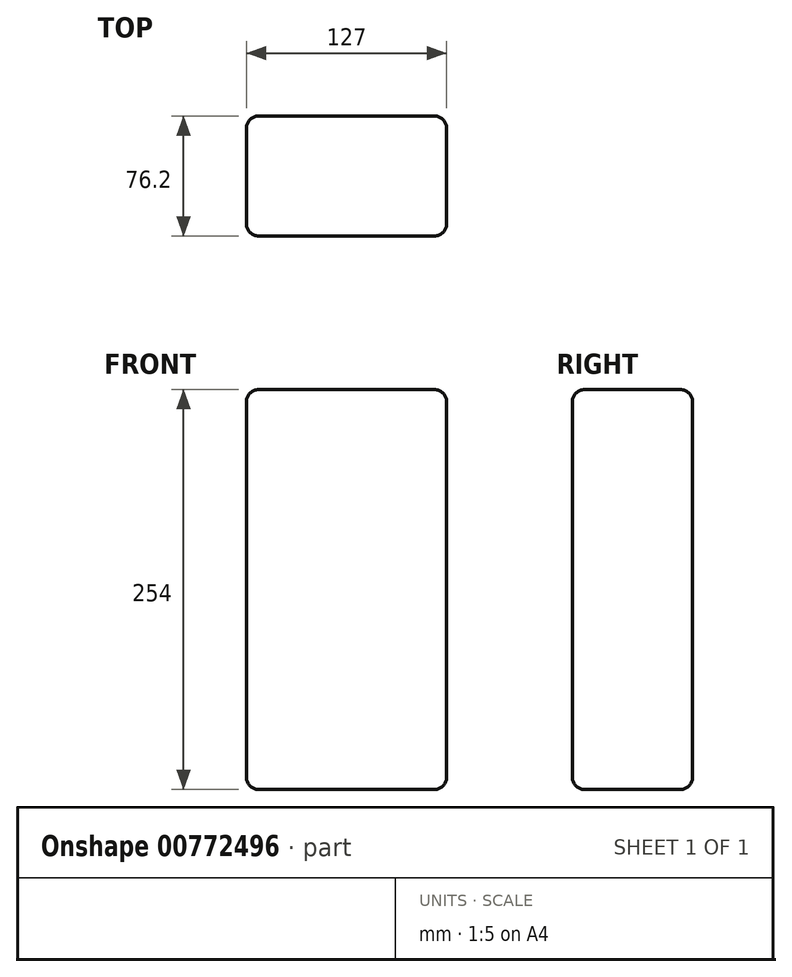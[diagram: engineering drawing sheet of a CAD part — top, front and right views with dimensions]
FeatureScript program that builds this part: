
annotation { "Feature Type Name" : "Feature", "Feature Type Description" : "" }
export const myFeature = defineFeature(function(context is Context, id is Id, definition is map)
    precondition{}
    {
        {
            var Q0;
            Q0=qCreatedBy(makeId("Front.planeOp"),FACE);
            var sketch = newSketch(context, id + "F0", { "sketchPlane" : qUnion([Q0])});
            skLineSegment(sketch, "E0.bottom", {"start": v(63.5, 127) * mm, "end": v(-63.5, 127) * mm});
            skLineSegment(sketch, "E0.top", {"start": v(63.5, -127) * mm, "end": v(-63.5, -127) * mm});
            skLineSegment(sketch, "E0.left", {"start": v(63.5, 127) * mm, "end": v(63.5, -127) * mm});
            skLineSegment(sketch, "E0.right", {"start": v(-63.5, 127) * mm, "end": v(-63.5, -127) * mm});
            skPoint(sketch, "E0.middle", {"position": v(0, 0) * mm});
            skSolve(sketch);
        }
        {
            var Q0;
            Q0=makeQuery(id+"F0.imprint","IMPRINT",FACE,{"disambiguationData":[TD([[makeQuery(id+"F0.imprint","IMPRINT",EDGE,{"derivedFrom":sQuery(id+"F0.wireOp",EDGE,"E0.bottom")}),1.0]])]});
            extrude(context, id + "F1", {"entities" : qUnion([Q0]), "depth" : 76.2 * mm, "offsetDistance" : 25.4 * mm});
        }
        {
            var Q0;
            Q0=makeQuery(id+"F1.opExtrude","CAP_EDGE",EDGE,{"disambiguationData":[OSD([sQuery(id+"F0.wireOp",EDGE,"E0.right")])],"isStart":false});
            var Q1;
            Q1=makeQuery(id+"F1.opExtrude","CAP_EDGE",EDGE,{"disambiguationData":[OSD([sQuery(id+"F0.wireOp",EDGE,"E0.right")])],"isStart":true});
            var Q2;
            Q2=makeQuery(id+"F1.opExtrude","SWEPT_EDGE",EDGE,{"disambiguationData":[OSD([sQuery(id+"F0.wireOp",EDGE,"E0.top"),sQuery(id+"F0.wireOp",EDGE,"E0.right")])]});
            var Q3;
            Q3=makeQuery(id+"F1.opExtrude","SWEPT_EDGE",EDGE,{"disambiguationData":[OSD([sQuery(id+"F0.wireOp",EDGE,"E0.bottom"),sQuery(id+"F0.wireOp",EDGE,"E0.right")])]});
            var Q4;
            Q4=makeQuery(id+"F1.opExtrude","SWEPT_EDGE",EDGE,{"disambiguationData":[OSD([sQuery(id+"F0.wireOp",EDGE,"E0.top"),sQuery(id+"F0.wireOp",EDGE,"E0.left")])]});
            var Q5;
            Q5=makeQuery(id+"F1.opExtrude","SWEPT_EDGE",EDGE,{"disambiguationData":[OSD([sQuery(id+"F0.wireOp",EDGE,"E0.bottom"),sQuery(id+"F0.wireOp",EDGE,"E0.left")])]});
            var Q6;
            Q6=makeQuery(id+"F1.opExtrude","CAP_EDGE",EDGE,{"disambiguationData":[OSD([sQuery(id+"F0.wireOp",EDGE,"E0.left")])],"isStart":false});
            var Q7;
            Q7=makeQuery(id+"F1.opExtrude","CAP_EDGE",EDGE,{"disambiguationData":[OSD([sQuery(id+"F0.wireOp",EDGE,"E0.top")])],"isStart":false});
            var Q8;
            Q8=makeQuery(id+"F1.opExtrude","CAP_EDGE",EDGE,{"disambiguationData":[OSD([sQuery(id+"F0.wireOp",EDGE,"E0.top")])],"isStart":true});
            var Q9;
            Q9=makeQuery(id+"F1.opExtrude","CAP_EDGE",EDGE,{"disambiguationData":[OSD([sQuery(id+"F0.wireOp",EDGE,"E0.left")])],"isStart":true});
            var Q10;
            Q10=makeQuery(id+"F1.opExtrude","CAP_EDGE",EDGE,{"disambiguationData":[OSD([sQuery(id+"F0.wireOp",EDGE,"E0.bottom")])],"isStart":true});
            var Q11;
            Q11=makeQuery(id+"F1.opExtrude","CAP_EDGE",EDGE,{"disambiguationData":[OSD([sQuery(id+"F0.wireOp",EDGE,"E0.bottom")])],"isStart":false});
            fillet(context, id + "F2", {"entities" : qUnion([Q0, Q1, Q2, Q3, Q4, Q5, Q6, Q7, Q8, Q9, Q10, Q11]), "radius" : 7.62 * mm, "tangentPropagation" : true, "allowEdgeOverflow" : false});
        }
    });
